# Revit family: Domotics-DomesticRanges-GEWISS-27COMBI_SYSTEM-IP55_COMMAND_2M
name_source: partatom
category: Apparecchi elettrici
revit_build: Autodesk Revit 2016 (Build: 20161004_0715(x64)
units: mm (PartAtom-declared; Revit-internal decimal feet)

## family parameters
Condiviso = Sì
Host = Superficie
Mantenere orientamento annotazione = Sì
Numero OmniClass = 23.80.30.14.24
Punto di calcolo locali = No
Quota connettore circolare = Usa diametro
Taglio con vuoti quando caricato = Sì
Tipo di parte = Normale
Titolo OmniClass = Junction Boxes

## types (1)
- Domotics-DomesticRanges-GEWISS-27COMBI_SYSTEM-IP55_COMMAND_2M
    Catalogue = DOMOTICS
    Catalogue Range = 27COMBI
    Colour = Grey RAL 7035
    Description: = 2 x Two-way switch 1P - 16AX
    Descrizione = 16AX 2-WAY SWITCH+2-WAY SWITCH IP55
    Door colour: = Transparent
    Door type = With membrane
    EAN code = 8011564074613
    Electrocod = 0130
    Glow Wire Test = 650°C
    IDF = a18e2113-a85a-4dd5-829a-3ecf7b41da5e
    IDT = 14f74f36-4a9b-4711-b464-f09deef8db8a
    IP degree = IP55
    Immagine tipo = GW27834.jpg
    Installation temperature = -25 +60 °C
    Insulation class = II
    Lid screws = Stainless steel
    Modello = GW27834
    N. holes Ã˜ 23 with cable gland = 1
    No. knockout holes Ã˜23 = 3 on sides / 1 on the bottom
    Offset = 0 mm  [stored 0 ft]
    Outer dim. LxHxD (mm) = 66x82x65
    Produttore = GEWISS S.p.A.
    Prospetto di default = 1219 mm
    SEO = Enclosure
    Standard; = EN 60669-1
    Technical sheet = https://www.gewiss.com
    Thermo-pressure with ball = 70
    Tipo simbolo = SIMBOLO DEVIATORI : DEVDOPPIO
    Torque screws tightening = 0,8NM
    Type = 2 x Two-way switch 1P - 16AX
    Type of knockout holes = Removable with tool
    URL = https://www.gewiss.com
    Version file RFA = 19.4
    Voltage = 230V ac
    Voltage: = 250 V ac

note: source unit labels omitted for Thermo-pressure with ball — the stored unit's dimension contradicts the parameter name (converter mislabeling)

note: [stored X ft] marks values corroborated as IEEE doubles in the binary element streams (Revit-internal decimal feet)

## geometry (parser evidence)
native form markers: Sweep x2
no freeform markers — native parametric forms only
